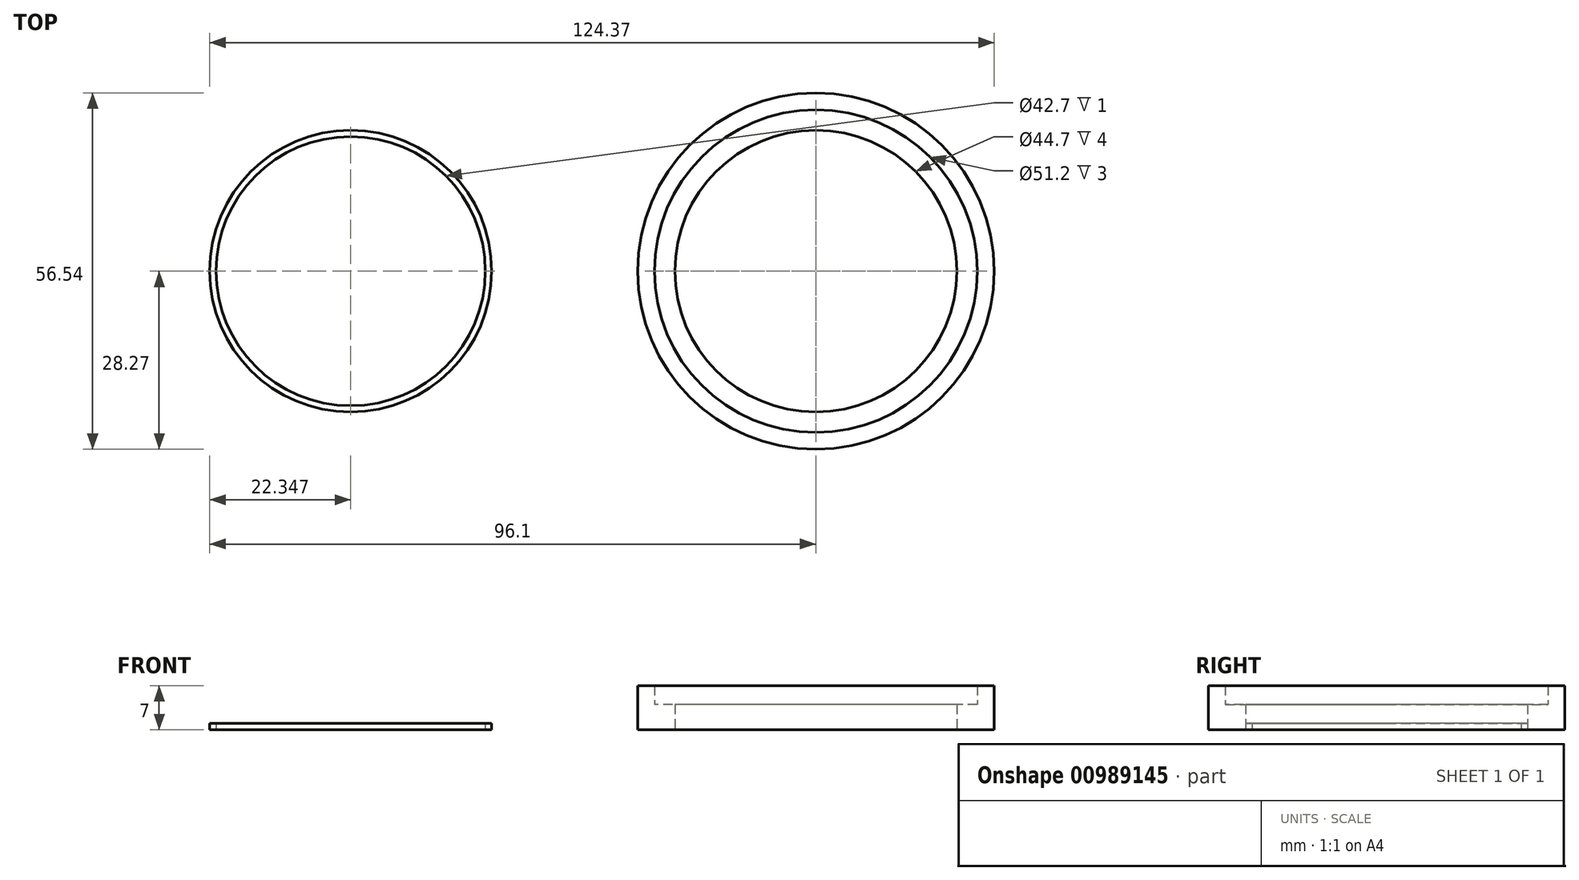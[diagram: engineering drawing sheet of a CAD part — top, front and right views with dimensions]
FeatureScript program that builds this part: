
annotation { "Feature Type Name" : "Feature", "Feature Type Description" : "" }
export const myFeature = defineFeature(function(context is Context, id is Id, definition is map)
    precondition{}
    {
        {
            var Q0;
            Q0=qCreatedBy(makeId("Top.planeOp"),FACE);
            var sketch = newSketch(context, id + "F0", { "sketchPlane" : qUnion([Q0])});
            skCircle(sketch, "E0", {"center": v(0, 0) * mm, "radius": 22.35 * mm});
            skCircle(sketch, "E1", {"center": v(0, 0) * mm, "radius": 25.6 * mm});
            skCircle(sketch, "E2", {"center": v(0, 0) * mm, "radius": 28.27 * mm});
            skCircle(sketch, "E3", {"center": v(-73.75, 0) * mm, "radius": 22.35 * mm});
            skCircle(sketch, "E4", {"center": v(-73.75, 0) * mm, "radius": 21.35 * mm});
            skSolve(sketch);
        }
        {
            var Q0;
            Q0=makeQuery(id+"F0.imprint","IMPRINT",FACE,{"disambiguationData":[TD([[makeQuery(id+"F0.imprint","IMPRINT",EDGE,{"derivedFrom":sQuery(id+"F0.wireOp",EDGE,"E0")}),-1.0]])]});
            extrude(context, id + "F1", {"entities" : qUnion([Q0]), "depth" : 4 * mm, "offsetDistance" : 25.4 * mm});
        }
        {
            var Q0;
            Q0=makeQuery(id+"F0.imprint","IMPRINT",FACE,{"disambiguationData":[TD([[makeQuery(id+"F0.imprint","IMPRINT",EDGE,{"derivedFrom":sQuery(id+"F0.wireOp",EDGE,"E1")}),-1.0]])]});
            extrude(context, id + "F2", {"entities" : qUnion([Q0]), "operationType" : NewBodyOperationType.ADD, "depth" : 7 * mm, "offsetDistance" : 25.4 * mm});
        }
        {
            var Q0;
            Q0=makeQuery(id+"F0.imprint","IMPRINT",FACE,{"disambiguationData":[TD([[makeQuery(id+"F0.imprint","IMPRINT",EDGE,{"derivedFrom":sQuery(id+"F0.wireOp",EDGE,"E3")}),1.0]])]});
            extrude(context, id + "F3", {"entities" : qUnion([Q0]), "depth" : 1 * mm, "offsetDistance" : 25.4 * mm});
        }
    });
